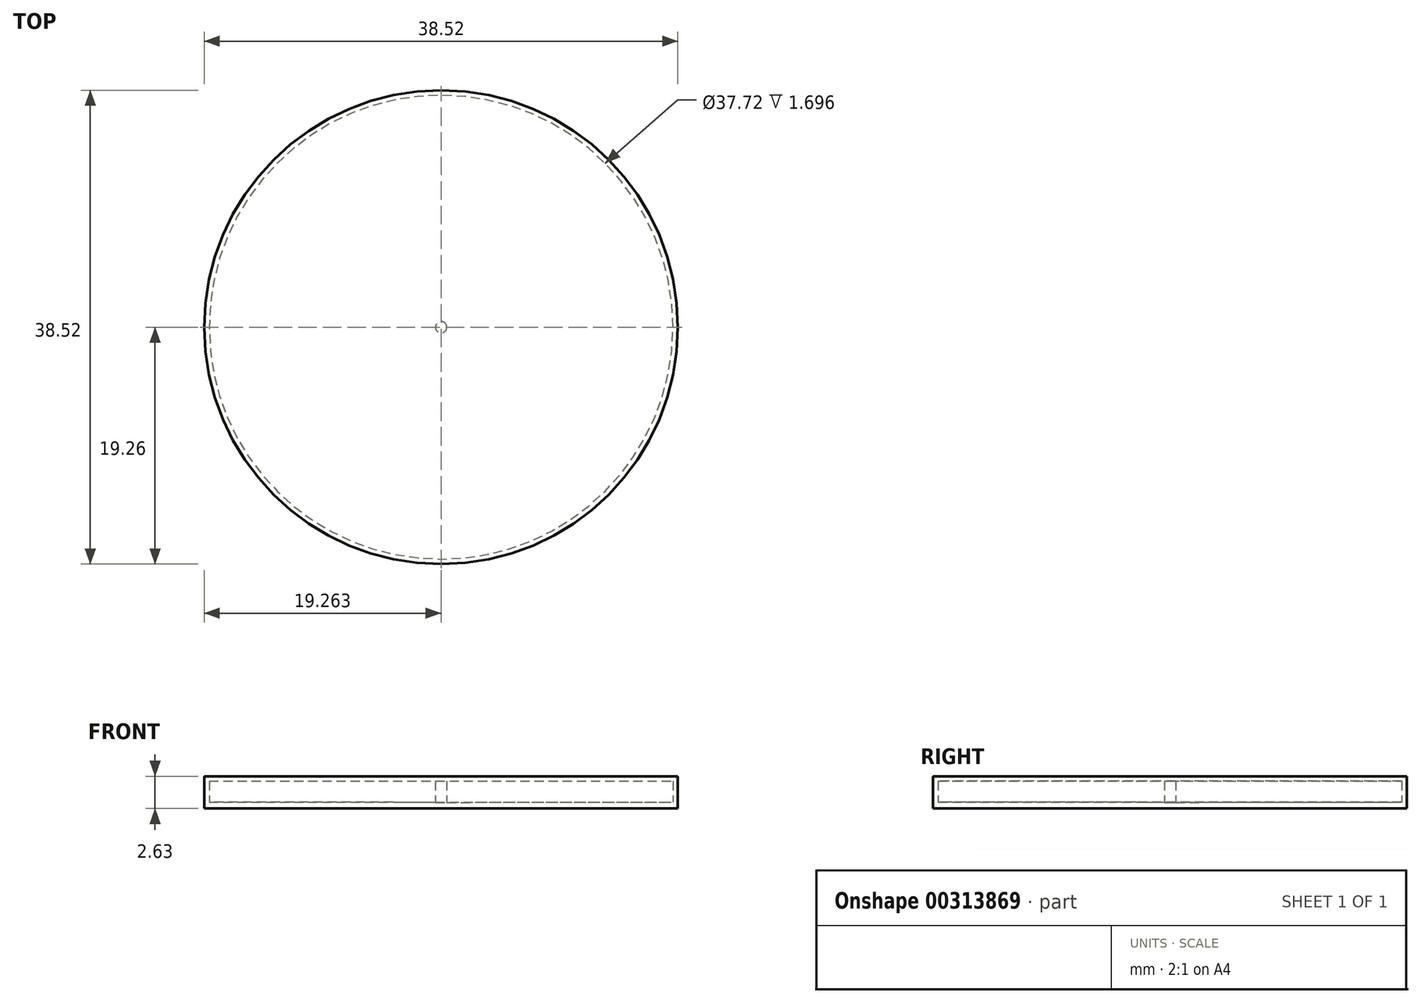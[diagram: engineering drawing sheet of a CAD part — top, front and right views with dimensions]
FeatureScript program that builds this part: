
annotation { "Feature Type Name" : "Feature", "Feature Type Description" : "" }
export const myFeature = defineFeature(function(context is Context, id is Id, definition is map)
    precondition{}
    {
        {
            var Q0;
            Q0=qCreatedBy(makeId("Front.planeOp"),FACE);
            var sketch = newSketch(context, id + "F0", { "sketchPlane" : qUnion([Q0])});
            skLineSegment(sketch, "E0.bottom", {"start": v(2.23, 0) * mm, "end": v(21.5, 0) * mm});
            skLineSegment(sketch, "E0.top", {"start": v(2.23, 2.63) * mm, "end": v(21.5, 2.63) * mm});
            skLineSegment(sketch, "E0.left", {"start": v(2.23, 0) * mm, "end": v(2.23, 2.63) * mm});
            skLineSegment(sketch, "E0.right", {"start": v(21.5, 0) * mm, "end": v(21.5, 2.63) * mm});
            skLineSegment(sketch, "E1", {"start": v(2.7, 0.5) * mm, "end": v(2.7, 2.22) * mm});
            skLineSegment(sketch, "E2", {"start": v(2.7, 2.22) * mm, "end": v(21.1, 2.22) * mm});
            skLineSegment(sketch, "E3", {"start": v(21.1, 2.22) * mm, "end": v(21.1, 0.53) * mm});
            skLineSegment(sketch, "E4", {"start": v(21.1, 0.53) * mm, "end": v(2.7, 0.5) * mm});
            skSolve(sketch);
        }
        {
            var Q0;
            Q0=makeQuery(id+"F0.imprint","IMPRINT",FACE,{"disambiguationData":[TD([[makeQuery(id+"F0.imprint","IMPRINT",EDGE,{"derivedFrom":sQuery(id+"F0.wireOp",EDGE,"E0.bottom")}),1.0]])]});
            var Q1;
            Q1=sQuery(id+"F0.wireOp",EDGE,"E0.left");
            revolve(context, id + "F1", {"entities" : qUnion([Q0]), "axis" : qUnion([Q1]), "revolveType" : RevolveType.FULL});
        }
    });
